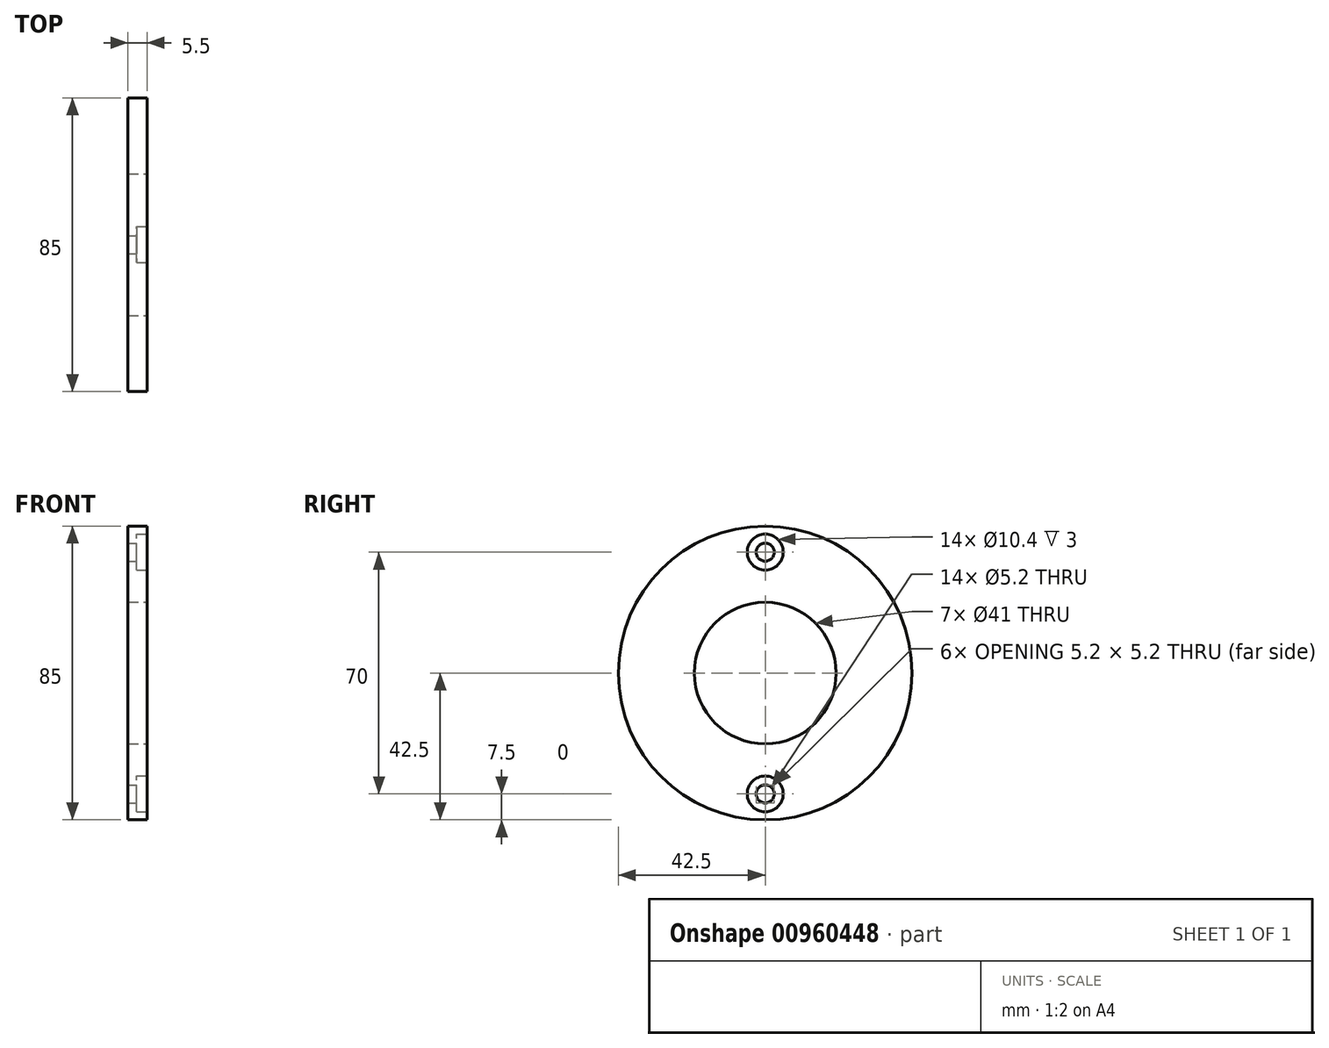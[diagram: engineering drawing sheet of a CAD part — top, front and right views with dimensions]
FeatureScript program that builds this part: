
annotation { "Feature Type Name" : "Feature", "Feature Type Description" : "" }
export const myFeature = defineFeature(function(context is Context, id is Id, definition is map)
    precondition{}
    {
        {
            var Q0;
            Q0=qCreatedBy(makeId("Front.planeOp"),FACE);
            var sketch = newSketch(context, id + "F0", { "sketchPlane" : qUnion([Q0])});
            skLineSegment(sketch, "E0.bottom", {"start": v(7.95, 42.5) * mm, "end": v(2.45, 42.5) * mm});
            skLineSegment(sketch, "E0.top", {"start": v(7.95, 20.5) * mm, "end": v(2.45, 20.5) * mm});
            skLineSegment(sketch, "E0.left", {"start": v(7.95, 42.5) * mm, "end": v(7.95, 20.5) * mm});
            skLineSegment(sketch, "E0.right", {"start": v(2.45, 42.5) * mm, "end": v(2.45, 20.5) * mm});
            skLineSegment(sketch, "E1", {"start": v(0, 0) * mm, "end": v(-9.37, 0) * mm});
            skSolve(sketch);
        }
        {
            var Q0;
            Q0=qSketchRegion(id+"F0",true);
            var Q1;
            Q1=sQuery(id+"F0.wireOp",EDGE,"E1");
            revolve(context, id + "F1", {"surfaceOperationType" : NewSurfaceOperationType.NEW, "entities" : qUnion([Q0]), "axis" : qUnion([Q1]), "revolveType" : RevolveType.FULL});
        }
        {
            var Q0;
            Q0=makeQuery(id+"F1.opRevolve","SWEPT_FACE",FACE,{"disambiguationData":[OSD([sQuery(id+"F0.wireOp",EDGE,"E0.left")])]});
            var sketch = newSketch(context, id + "F2", { "sketchPlane" : qUnion([Q0])});
            skCircle(sketch, "E2", {"center": v(0, 35) * mm, "radius": 5.2 * mm});
            skCircle(sketch, "E3", {"center": v(0, -35) * mm, "radius": 5.2 * mm});
            skSolve(sketch);
        }
        {
            var Q0;
            Q0 = qSketchRegion(id + "F2", true);
            extrude(context, id + "F3", {"entities" : qUnion([Q0]), "operationType" : NewBodyOperationType.REMOVE, "oppositeDirection" : true, "depth" : 3 * mm, "offsetDistance" : 25 * mm});
        }
        {
            var Q0;
            Q0=makeQuery(id+"F3.boolean.opBoolean","COPY",FACE,{"derivedFrom":makeQuery(id+"F3.opExtrude","CAP_FACE",FACE,{"disambiguationData":[OSD([sQuery(id+"F2.wireOp",EDGE,"E2")])],"isStart":false})});
            var sketch = newSketch(context, id + "F4", { "sketchPlane" : qUnion([Q0])});
            skCircle(sketch, "E4", {"center": v(0, 35) * mm, "radius": 2.6 * mm});
            skCircle(sketch, "E5.1.0", {"center": v(0, -35) * mm, "radius": 2.6 * mm});
            skPoint(sketch, "E5.center", {"position": v(0, 0) * mm});
            skSolve(sketch);
        }
        {
            var Q0;
            Q0 = qSketchRegion(id + "F4", true);
            extrude(context, id + "F5", {"entities" : qUnion([Q0]), "operationType" : NewBodyOperationType.REMOVE, "oppositeDirection" : true, "depth" : 25 * mm, "offsetDistance" : 25 * mm});
        }
    });
